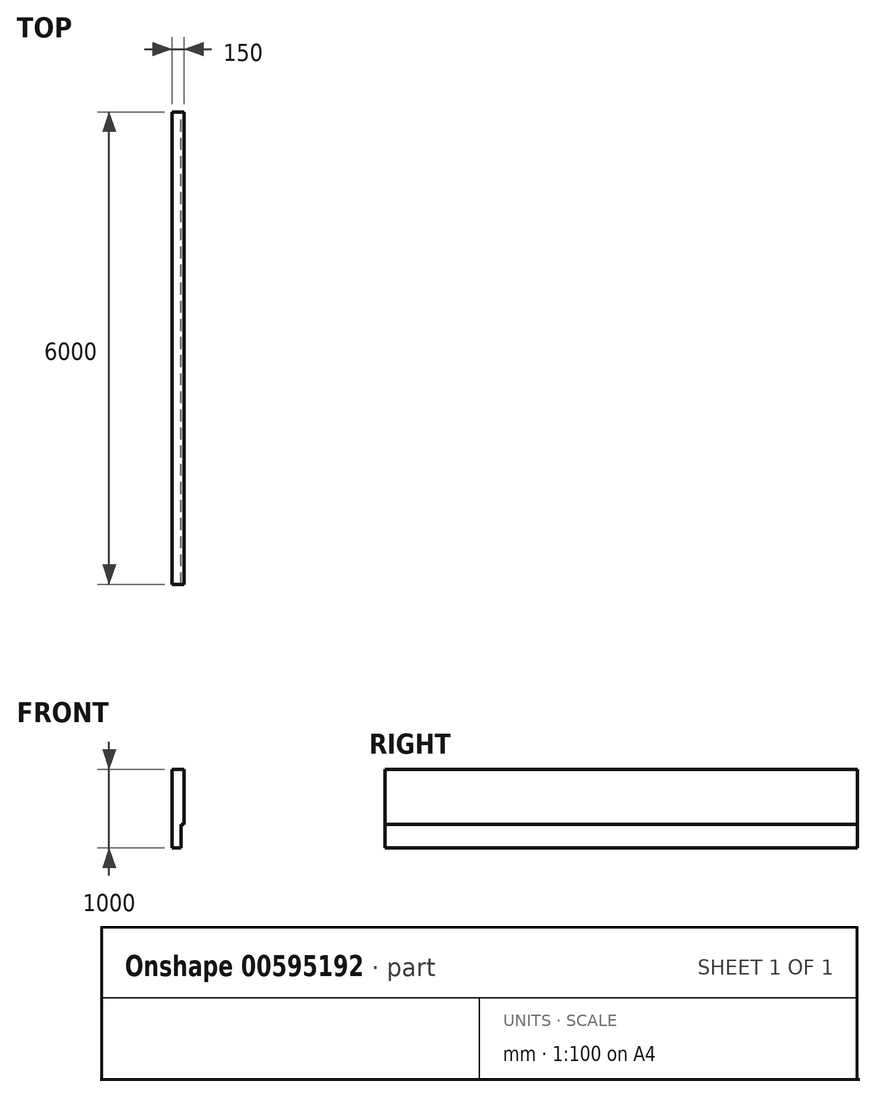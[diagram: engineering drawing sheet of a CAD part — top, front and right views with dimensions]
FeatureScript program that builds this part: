
annotation { "Feature Type Name" : "Feature", "Feature Type Description" : "" }
export const myFeature = defineFeature(function(context is Context, id is Id, definition is map)
    precondition{}
    {
        {
            var Q0;
            Q0=qCreatedBy(makeId("Front.planeOp"),FACE);
            var sketch = newSketch(context, id + "F0", { "sketchPlane" : qUnion([Q0])});
            skLineSegment(sketch, "E0", {"start": v(-100, 1000) * mm, "end": v(-100, 0) * mm});
            skLineSegment(sketch, "E1", {"start": v(-100, 1000) * mm, "end": v(50, 1000) * mm});
            skLineSegment(sketch, "E2", {"start": v(50, 1000) * mm, "end": v(50, 300) * mm});
            skLineSegment(sketch, "E3", {"start": v(50, 300) * mm, "end": v(10, 300) * mm});
            skLineSegment(sketch, "E4", {"start": v(10, 300) * mm, "end": v(10, 0) * mm});
            skLineSegment(sketch, "E5", {"start": v(10, 0) * mm, "end": v(-100, 0) * mm});
            skSolve(sketch);
        }
        {
            var Q0;
            Q0 = qSketchRegion(id + "F0", true);
            extrude(context, id + "F1", {"entities" : qUnion([Q0]), "depth" : 6000 * mm, "offsetDistance" : 25 * mm});
        }
    });
